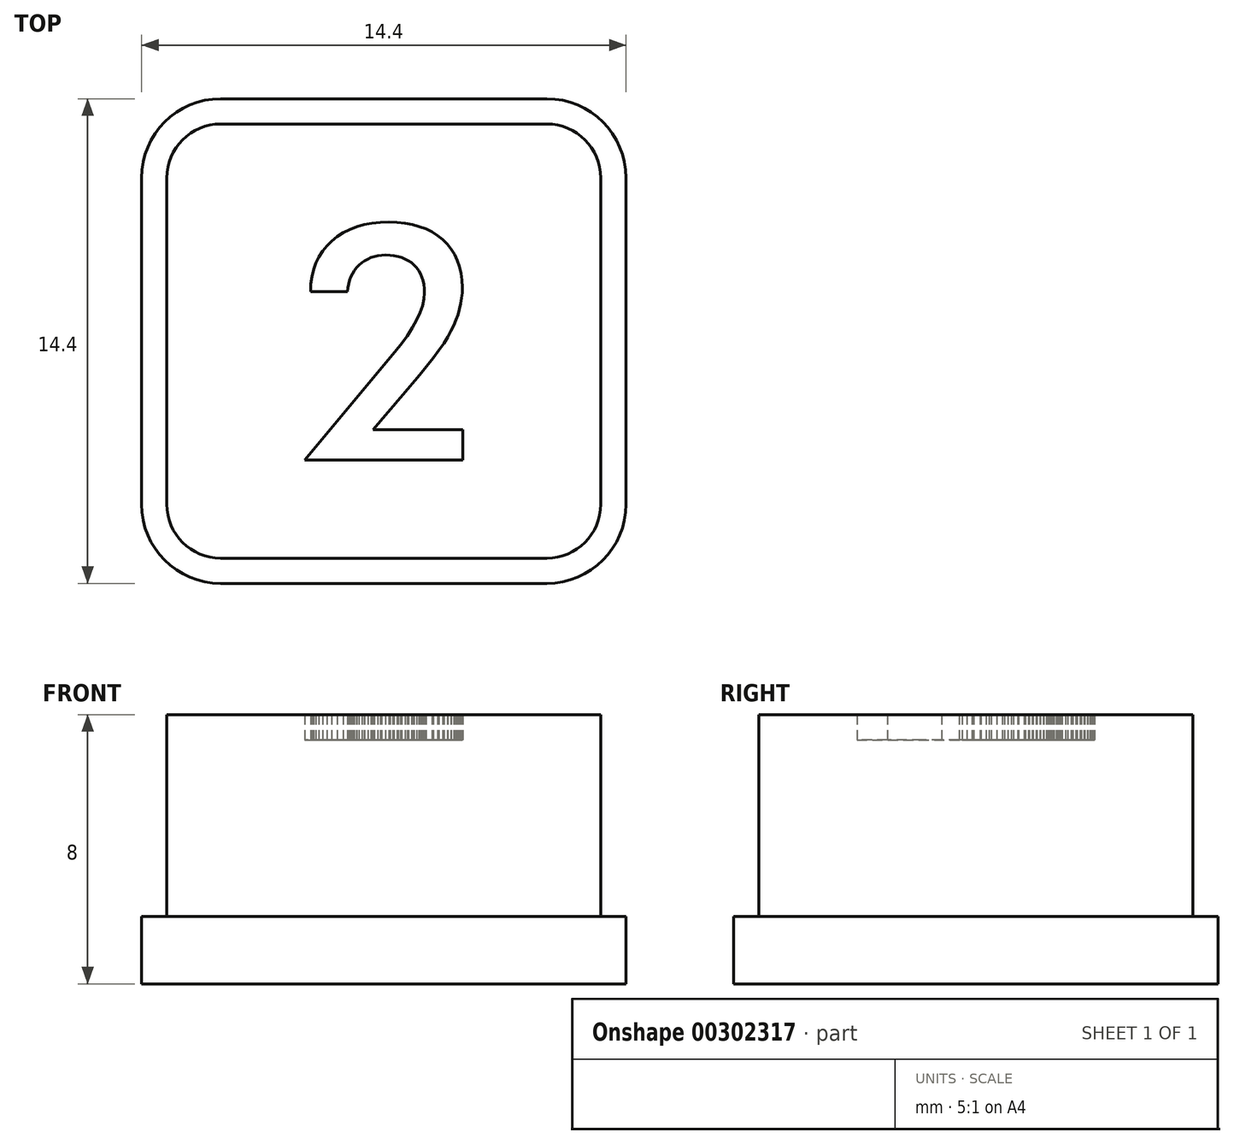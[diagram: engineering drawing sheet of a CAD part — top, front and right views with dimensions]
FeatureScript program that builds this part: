
annotation { "Feature Type Name" : "Feature", "Feature Type Description" : "" }
export const myFeature = defineFeature(function(context is Context, id is Id, definition is map)
    precondition{}
    {
        {
            var Q0;
            Q0=qCreatedBy(makeId("Top.planeOp"),FACE);
            var sketch = newSketch(context, id + "F0", { "sketchPlane" : qUnion([Q0])});
            skLineSegment(sketch, "E0", {"start": v(2.35, -2.63) * mm, "end": v(2.35, -3.54) * mm});
            skLineSegment(sketch, "E1", {"start": v(2.35, -3.54) * mm, "end": v(-2.35, -3.54) * mm});
            skLineSegment(sketch, "E2", {"start": v(-2.35, -3.54) * mm, "end": v(0.27, -0.4) * mm});
            skLineSegment(sketch, "E3", {"start": v(0.27, -0.4) * mm, "end": v(0.5, -0.12) * mm});
            skLineSegment(sketch, "E4", {"start": v(0.5, -0.12) * mm, "end": v(0.7, 0.15) * mm});
            skLineSegment(sketch, "E5", {"start": v(0.7, 0.15) * mm, "end": v(0.85, 0.4) * mm});
            skLineSegment(sketch, "E6", {"start": v(0.85, 0.4) * mm, "end": v(0.98, 0.63) * mm});
            skLineSegment(sketch, "E7", {"start": v(0.98, 0.63) * mm, "end": v(1.08, 0.85) * mm});
            skLineSegment(sketch, "E8", {"start": v(1.08, 0.85) * mm, "end": v(1.15, 1.05) * mm});
            skLineSegment(sketch, "E9", {"start": v(1.15, 1.05) * mm, "end": v(1.2, 1.25) * mm});
            skLineSegment(sketch, "E10", {"start": v(1.2, 1.25) * mm, "end": v(1.2, 1.44) * mm});
            skLineSegment(sketch, "E11", {"start": v(1.2, 1.44) * mm, "end": v(1.2, 1.56) * mm});
            skLineSegment(sketch, "E12", {"start": v(1.2, 1.56) * mm, "end": v(1.19, 1.68) * mm});
            skLineSegment(sketch, "E13", {"start": v(1.19, 1.68) * mm, "end": v(1.16, 1.8) * mm});
            skLineSegment(sketch, "E14", {"start": v(1.16, 1.8) * mm, "end": v(1.13, 1.9) * mm});
            skLineSegment(sketch, "E15", {"start": v(1.13, 1.9) * mm, "end": v(1.09, 2) * mm});
            skLineSegment(sketch, "E16", {"start": v(1.09, 2) * mm, "end": v(1.03, 2.1) * mm});
            skLineSegment(sketch, "E17", {"start": v(1.03, 2.1) * mm, "end": v(0.97, 2.18) * mm});
            skLineSegment(sketch, "E18", {"start": v(0.97, 2.18) * mm, "end": v(0.9, 2.26) * mm});
            skLineSegment(sketch, "E19", {"start": v(0.9, 2.26) * mm, "end": v(0.82, 2.33) * mm});
            skLineSegment(sketch, "E20", {"start": v(0.82, 2.33) * mm, "end": v(0.73, 2.39) * mm});
            skLineSegment(sketch, "E21", {"start": v(0.73, 2.39) * mm, "end": v(0.64, 2.44) * mm});
            skLineSegment(sketch, "E22", {"start": v(0.64, 2.44) * mm, "end": v(0.53, 2.48) * mm});
            skLineSegment(sketch, "E23", {"start": v(0.53, 2.48) * mm, "end": v(0.42, 2.51) * mm});
            skLineSegment(sketch, "E24", {"start": v(0.42, 2.51) * mm, "end": v(0.3, 2.54) * mm});
            skLineSegment(sketch, "E25", {"start": v(0.3, 2.54) * mm, "end": v(0.19, 2.55) * mm});
            skLineSegment(sketch, "E26", {"start": v(0.19, 2.55) * mm, "end": v(0.05, 2.56) * mm});
            skLineSegment(sketch, "E27", {"start": v(0.05, 2.56) * mm, "end": v(-0.06, 2.55) * mm});
            skLineSegment(sketch, "E28", {"start": v(-0.06, 2.55) * mm, "end": v(-0.17, 2.54) * mm});
            skLineSegment(sketch, "E29", {"start": v(-0.17, 2.54) * mm, "end": v(-0.28, 2.51) * mm});
            skLineSegment(sketch, "E30", {"start": v(-0.28, 2.51) * mm, "end": v(-0.38, 2.48) * mm});
            skLineSegment(sketch, "E31", {"start": v(-0.38, 2.48) * mm, "end": v(-0.48, 2.44) * mm});
            skLineSegment(sketch, "E32", {"start": v(-0.48, 2.44) * mm, "end": v(-0.57, 2.39) * mm});
            skLineSegment(sketch, "E33", {"start": v(-0.57, 2.39) * mm, "end": v(-0.65, 2.33) * mm});
            skLineSegment(sketch, "E34", {"start": v(-0.65, 2.33) * mm, "end": v(-0.73, 2.26) * mm});
            skLineSegment(sketch, "E35", {"start": v(-0.73, 2.26) * mm, "end": v(-0.8, 2.18) * mm});
            skLineSegment(sketch, "E36", {"start": v(-0.8, 2.18) * mm, "end": v(-0.87, 2.1) * mm});
            skLineSegment(sketch, "E37", {"start": v(-0.87, 2.1) * mm, "end": v(-0.93, 2) * mm});
            skLineSegment(sketch, "E38", {"start": v(-0.93, 2) * mm, "end": v(-0.98, 1.91) * mm});
            skLineSegment(sketch, "E39", {"start": v(-0.98, 1.91) * mm, "end": v(-1.02, 1.8) * mm});
            skLineSegment(sketch, "E40", {"start": v(-1.02, 1.8) * mm, "end": v(-1.05, 1.7) * mm});
            skLineSegment(sketch, "E41", {"start": v(-1.05, 1.7) * mm, "end": v(-1.07, 1.59) * mm});
            skLineSegment(sketch, "E42", {"start": v(-1.07, 1.59) * mm, "end": v(-1.08, 1.47) * mm});
            skLineSegment(sketch, "E43", {"start": v(-1.08, 1.47) * mm, "end": v(-2.18, 1.47) * mm});
            skLineSegment(sketch, "E44", {"start": v(-2.18, 1.47) * mm, "end": v(-2.17, 1.7) * mm});
            skLineSegment(sketch, "E45", {"start": v(-2.17, 1.7) * mm, "end": v(-2.14, 1.92) * mm});
            skLineSegment(sketch, "E46", {"start": v(-2.14, 1.92) * mm, "end": v(-2.09, 2.12) * mm});
            skLineSegment(sketch, "E47", {"start": v(-2.09, 2.12) * mm, "end": v(-2.02, 2.32) * mm});
            skLineSegment(sketch, "E48", {"start": v(-2.02, 2.32) * mm, "end": v(-1.93, 2.5) * mm});
            skLineSegment(sketch, "E49", {"start": v(-1.93, 2.5) * mm, "end": v(-1.82, 2.67) * mm});
            skLineSegment(sketch, "E50", {"start": v(-1.82, 2.67) * mm, "end": v(-1.7, 2.83) * mm});
            skLineSegment(sketch, "E51", {"start": v(-1.7, 2.83) * mm, "end": v(-1.55, 2.97) * mm});
            skLineSegment(sketch, "E52", {"start": v(-1.55, 2.97) * mm, "end": v(-1.38, 3.1) * mm});
            skLineSegment(sketch, "E53", {"start": v(-1.38, 3.1) * mm, "end": v(-1.2, 3.22) * mm});
            skLineSegment(sketch, "E54", {"start": v(-1.2, 3.22) * mm, "end": v(-1.01, 3.32) * mm});
            skLineSegment(sketch, "E55", {"start": v(-1.01, 3.32) * mm, "end": v(-0.8, 3.4) * mm});
            skLineSegment(sketch, "E56", {"start": v(-0.8, 3.4) * mm, "end": v(-0.59, 3.46) * mm});
            skLineSegment(sketch, "E57", {"start": v(-0.59, 3.46) * mm, "end": v(-0.36, 3.5) * mm});
            skLineSegment(sketch, "E58", {"start": v(-0.36, 3.5) * mm, "end": v(-0.1, 3.53) * mm});
            skLineSegment(sketch, "E59", {"start": v(-0.1, 3.53) * mm, "end": v(0.15, 3.54) * mm});
            skLineSegment(sketch, "E60", {"start": v(0.15, 3.54) * mm, "end": v(0.4, 3.53) * mm});
            skLineSegment(sketch, "E61", {"start": v(0.4, 3.53) * mm, "end": v(0.63, 3.5) * mm});
            skLineSegment(sketch, "E62", {"start": v(0.63, 3.5) * mm, "end": v(0.85, 3.46) * mm});
            skLineSegment(sketch, "E63", {"start": v(0.85, 3.46) * mm, "end": v(1.06, 3.4) * mm});
            skLineSegment(sketch, "E64", {"start": v(1.06, 3.4) * mm, "end": v(1.25, 3.33) * mm});
            skLineSegment(sketch, "E65", {"start": v(1.25, 3.33) * mm, "end": v(1.43, 3.24) * mm});
            skLineSegment(sketch, "E66", {"start": v(1.43, 3.24) * mm, "end": v(1.6, 3.14) * mm});
            skLineSegment(sketch, "E67", {"start": v(1.6, 3.14) * mm, "end": v(1.75, 3.01) * mm});
            skLineSegment(sketch, "E68", {"start": v(1.75, 3.01) * mm, "end": v(1.89, 2.88) * mm});
            skLineSegment(sketch, "E69", {"start": v(1.89, 2.88) * mm, "end": v(2, 2.73) * mm});
            skLineSegment(sketch, "E70", {"start": v(2, 2.73) * mm, "end": v(2.1, 2.57) * mm});
            skLineSegment(sketch, "E71", {"start": v(2.1, 2.57) * mm, "end": v(2.19, 2.4) * mm});
            skLineSegment(sketch, "E72", {"start": v(2.19, 2.4) * mm, "end": v(2.25, 2.22) * mm});
            skLineSegment(sketch, "E73", {"start": v(2.25, 2.22) * mm, "end": v(2.3, 2.02) * mm});
            skLineSegment(sketch, "E74", {"start": v(2.3, 2.02) * mm, "end": v(2.33, 1.81) * mm});
            skLineSegment(sketch, "E75", {"start": v(2.33, 1.81) * mm, "end": v(2.34, 1.6) * mm});
            skLineSegment(sketch, "E76", {"start": v(2.34, 1.6) * mm, "end": v(2.33, 1.43) * mm});
            skLineSegment(sketch, "E77", {"start": v(2.33, 1.43) * mm, "end": v(2.31, 1.27) * mm});
            skLineSegment(sketch, "E78", {"start": v(2.31, 1.27) * mm, "end": v(2.29, 1.11) * mm});
            skLineSegment(sketch, "E79", {"start": v(2.29, 1.11) * mm, "end": v(2.25, 0.95) * mm});
            skLineSegment(sketch, "E80", {"start": v(2.25, 0.95) * mm, "end": v(2.2, 0.79) * mm});
            skLineSegment(sketch, "E81", {"start": v(2.2, 0.79) * mm, "end": v(2.15, 0.63) * mm});
            skLineSegment(sketch, "E82", {"start": v(2.15, 0.63) * mm, "end": v(2.08, 0.46) * mm});
            skLineSegment(sketch, "E83", {"start": v(2.08, 0.46) * mm, "end": v(2, 0.3) * mm});
            skLineSegment(sketch, "E84", {"start": v(2, 0.3) * mm, "end": v(1.9, 0.13) * mm});
            skLineSegment(sketch, "E85", {"start": v(1.9, 0.13) * mm, "end": v(1.78, -0.06) * mm});
            skLineSegment(sketch, "E86", {"start": v(1.78, -0.06) * mm, "end": v(1.64, -0.27) * mm});
            skLineSegment(sketch, "E87", {"start": v(1.64, -0.27) * mm, "end": v(1.47, -0.5) * mm});
            skLineSegment(sketch, "E88", {"start": v(1.47, -0.5) * mm, "end": v(1.07, -1) * mm});
            skLineSegment(sketch, "E89", {"start": v(1.07, -1) * mm, "end": v(0.57, -1.6) * mm});
            skLineSegment(sketch, "E90", {"start": v(0.57, -1.6) * mm, "end": v(-0.32, -2.63) * mm});
            skLineSegment(sketch, "E91", {"start": v(-0.32, -2.63) * mm, "end": v(2.35, -2.63) * mm});
            skArc(sketch, "E92", {"start": v(4.85, -6.45) * mm, "mid": v(5.98, -5.98) * mm, "end": v(6.45, -4.85) * mm});
            skLineSegment(sketch, "E93", {"start": v(6.45, -4.85) * mm, "end": v(6.45, 4.85) * mm});
            skArc(sketch, "E94", {"start": v(6.45, 4.85) * mm, "mid": v(5.98, 5.98) * mm, "end": v(4.85, 6.45) * mm});
            skLineSegment(sketch, "E95", {"start": v(4.85, 6.45) * mm, "end": v(-4.85, 6.45) * mm});
            skArc(sketch, "E96", {"start": v(-4.85, 6.45) * mm, "mid": v(-5.98, 5.98) * mm, "end": v(-6.45, 4.85) * mm});
            skLineSegment(sketch, "E97", {"start": v(-6.45, 4.85) * mm, "end": v(-6.45, -4.85) * mm});
            skArc(sketch, "E98", {"start": v(-6.45, -4.85) * mm, "mid": v(-5.98, -5.98) * mm, "end": v(-4.85, -6.45) * mm});
            skLineSegment(sketch, "E99", {"start": v(-4.85, -6.45) * mm, "end": v(4.85, -6.45) * mm});
            skArc(sketch, "E100", {"start": v(-4.85, 7.2) * mm, "mid": v(-6.51, 6.51) * mm, "end": v(-7.2, 4.85) * mm});
            skLineSegment(sketch, "E101", {"start": v(-7.2, 4.85) * mm, "end": v(-7.2, -4.85) * mm});
            skArc(sketch, "E102", {"start": v(-7.2, -4.85) * mm, "mid": v(-6.51, -6.51) * mm, "end": v(-4.85, -7.2) * mm});
            skLineSegment(sketch, "E103", {"start": v(-4.85, -7.2) * mm, "end": v(4.85, -7.2) * mm});
            skArc(sketch, "E104", {"start": v(4.85, -7.2) * mm, "mid": v(6.51, -6.51) * mm, "end": v(7.2, -4.85) * mm});
            skLineSegment(sketch, "E105", {"start": v(7.2, -4.85) * mm, "end": v(7.2, 4.85) * mm});
            skArc(sketch, "E106", {"start": v(7.2, 4.85) * mm, "mid": v(6.51, 6.51) * mm, "end": v(4.85, 7.2) * mm});
            skLineSegment(sketch, "E107", {"start": v(4.85, 7.2) * mm, "end": v(-4.85, 7.2) * mm});
            skSolve(sketch);
        }
        {
            var Q0;
            Q0 = qSketchRegion(id + "F0", true);
            extrude(context, id + "F1", {"entities" : qUnion([Q0]), "depth" : 2 * mm});
        }
        {
            var Q0;
            Q0=makeQuery(id+"F0.imprint","IMPRINT",FACE,{"disambiguationData":[TD([[makeQuery(id+"F0.imprint","IMPRINT",EDGE,{"derivedFrom":sQuery(id+"F0.wireOp",EDGE,"E0")}),1.0]])]});
            extrude(context, id + "F2", {"entities" : qUnion([Q0]), "operationType" : NewBodyOperationType.ADD, "depth" : 8 * mm});
        }
        {
            var Q0;
            Q0=makeQuery(id+"F0.imprint","IMPRINT",FACE,{"disambiguationData":[TD([[makeQuery(id+"F0.imprint","IMPRINT",EDGE,{"derivedFrom":sQuery(id+"F0.wireOp",EDGE,"E0")}),-1.0]])]});
            extrude(context, id + "F3", {"entities" : qUnion([Q0]), "operationType" : NewBodyOperationType.ADD, "depth" : 7.25 * mm});
        }
    });
